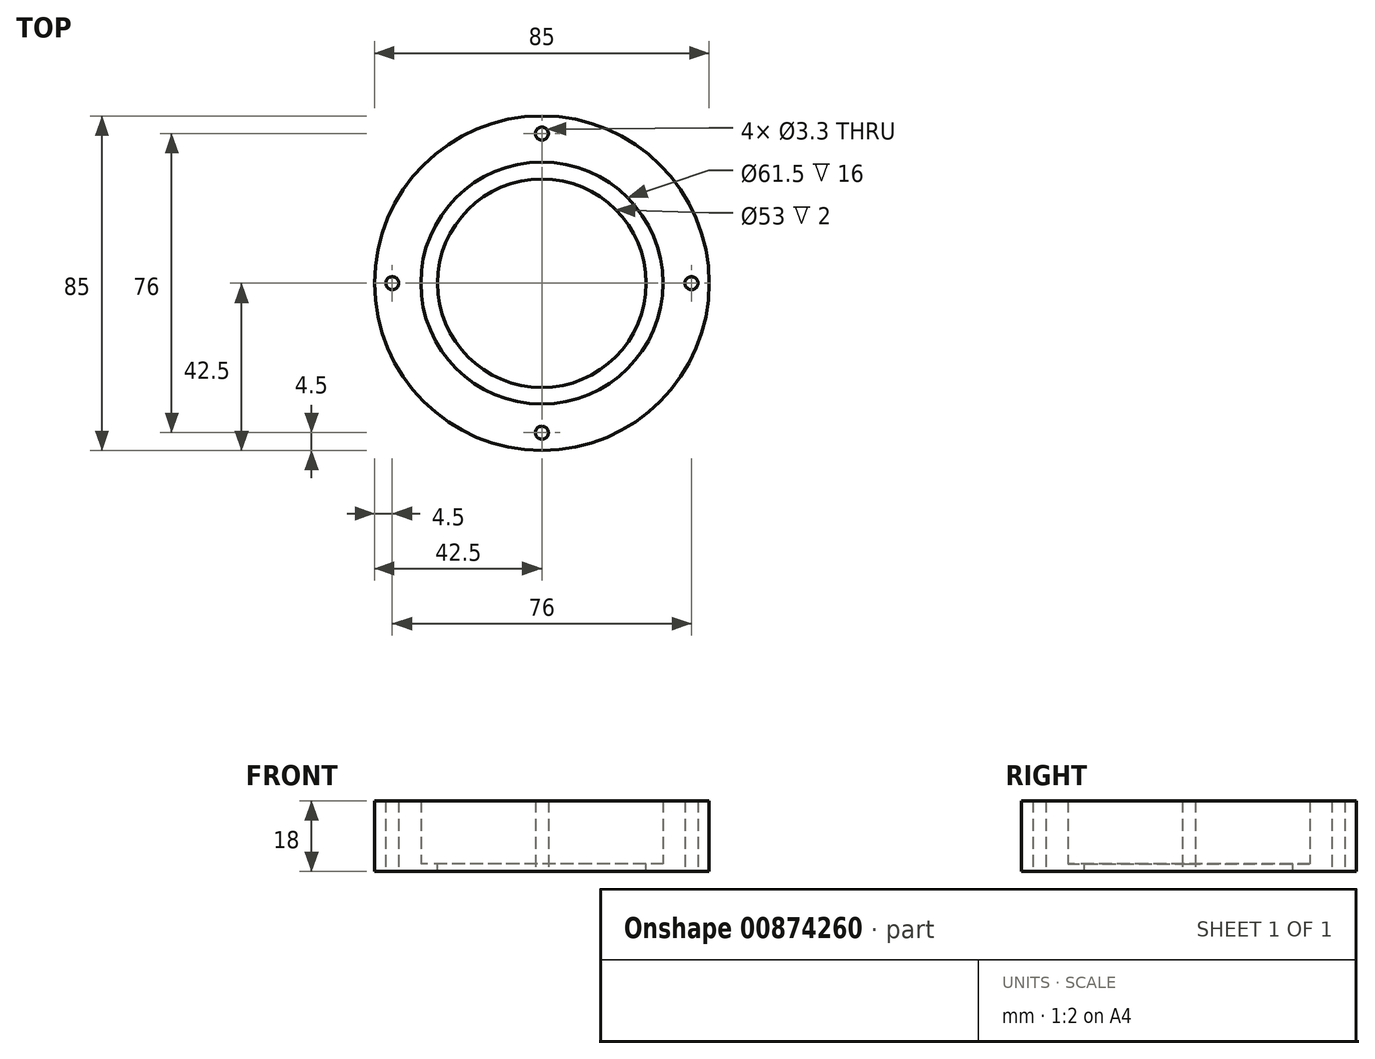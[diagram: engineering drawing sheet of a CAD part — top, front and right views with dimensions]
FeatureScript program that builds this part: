
annotation { "Feature Type Name" : "Feature", "Feature Type Description" : "" }
export const myFeature = defineFeature(function(context is Context, id is Id, definition is map)
    precondition{}
    {
        {
            var Q0;
            Q0=qCreatedBy(makeId("Top.planeOp"),FACE);
            var sketch = newSketch(context, id + "F0", { "sketchPlane" : qUnion([Q0])});
            skCircle(sketch, "E0", {"center": v(0, 0) * mm, "radius": 42.5 * mm});
            skCircle(sketch, "E1", {"center": v(0, 0) * mm, "radius": 30.75 * mm});
            skLineSegment(sketch, "E2", {"start": v(0, 0) * mm, "end": v(0, 38) * mm, "construction": true});
            skLineSegment(sketch, "E3", {"start": v(0, 0) * mm, "end": v(-38, 0) * mm, "construction": true});
            skLineSegment(sketch, "E4", {"start": v(0, 0) * mm, "end": v(0, -38) * mm, "construction": true});
            skLineSegment(sketch, "E5", {"start": v(0, 0) * mm, "end": v(38, 0) * mm, "construction": true});
            skCircle(sketch, "E6", {"center": v(38, 0) * mm, "radius": 1.65 * mm});
            skCircle(sketch, "E7", {"center": v(0, -38) * mm, "radius": 1.65 * mm});
            skCircle(sketch, "E8", {"center": v(-38, 0) * mm, "radius": 1.65 * mm});
            skCircle(sketch, "E9", {"center": v(0, 38) * mm, "radius": 1.65 * mm});
            skSolve(sketch);
        }
        {
            var Q0;
            Q0 = qSketchRegion(id + "F0", true);
            extrude(context, id + "F1", {"entities" : qUnion([Q0]), "depth" : 16 * mm, "offsetDistance" : 25 * mm});
        }
        {
            var Q0;
            Q0=qCreatedBy(makeId("Top.planeOp"),FACE);
            var sketch = newSketch(context, id + "F2", { "sketchPlane" : qUnion([Q0])});
            skCircle(sketch, "E10", {"center": v(0, 0) * mm, "radius": 42.5 * mm});
            skCircle(sketch, "E11", {"center": v(0, 0) * mm, "radius": 26.5 * mm});
            skLineSegment(sketch, "E12", {"start": v(0, 0) * mm, "end": v(38, 0) * mm, "construction": true});
            skLineSegment(sketch, "E13", {"start": v(0, 0) * mm, "end": v(0, 38) * mm, "construction": true});
            skLineSegment(sketch, "E14", {"start": v(0, 0) * mm, "end": v(-38, 0) * mm, "construction": true});
            skLineSegment(sketch, "E15", {"start": v(0, 0) * mm, "end": v(0, -38) * mm, "construction": true});
            skCircle(sketch, "E16", {"center": v(0, -38) * mm, "radius": 1.65 * mm});
            skCircle(sketch, "E17", {"center": v(38, 0) * mm, "radius": 1.65 * mm});
            skCircle(sketch, "E18", {"center": v(-38, 0) * mm, "radius": 1.65 * mm});
            skCircle(sketch, "E19", {"center": v(0, 38) * mm, "radius": 1.65 * mm});
            skSolve(sketch);
        }
        {
            var Q0;
            Q0 = qSketchRegion(id + "F2", true);
            extrude(context, id + "F3", {"entities" : qUnion([Q0]), "operationType" : NewBodyOperationType.ADD, "oppositeDirection" : true, "depth" : 2 * mm, "offsetDistance" : 25 * mm});
        }
    });
